# Revit family: Lacuna Plaza 12W
name_source: partatom
category: Lighting Fixtures
revit_build: Autodesk Revit 2016 (Build: 20150714_1515(x64)
units: mm (PartAtom-declared; Revit-internal decimal feet)

## family parameters
Cut with Voids When Loaded = No
Host = Face
Light Source = Yes
OmniClass Number = 23.80.70.14.11
OmniClass Title = Amenity Lighting
Part Type = Normal
Room Calculation Point = No
Round Connector Dimension = Use Diameter
Shared = No

## types (1)
- Lacuna Plaza 12W, Neutral White, White, 230V - 53UL392N012X
    Beam Angle = 120°
    CRI = 84
    Casing Color = White
    Color = White Metal
    Color Filter = 16777215
    Color Temperature = 4000K
    Cutout = -
    Default Elevation = 2300 mm
    Depth = -
    Description = Pathway light
    Dimensions = 150mm x 150mm x 600mm
    Dimmable = No
    Dimming Lamp Color Temperature Shift = <None>
    Directivity = No
    Driver = Integrated
    Housing Material = Aluminium
    IP Code = IP54
    Lamp = LED
    Last Updated = 28.2.2017
    Lifetime L70 = 50000h
    Lumens Output = 866lm
    Manufacturer = Winled Oy Ltd
    Model = Lacuna Plaza 12W
    Operating Temperature Range = -20° to +50°
    Photometric Web File = Lacuna Plaza 12W.ies
    Product Number = 53UL392N012X
    Tilt Angle = 90.00°
    Type Image = Lacuna Plaza 12W.png
    URL = www.winled.fi
    Voltage = 230 V
    Wattage Comments = 12W

## geometry (parser evidence)
native form markers: Sweep x6
no freeform markers — native parametric forms only
